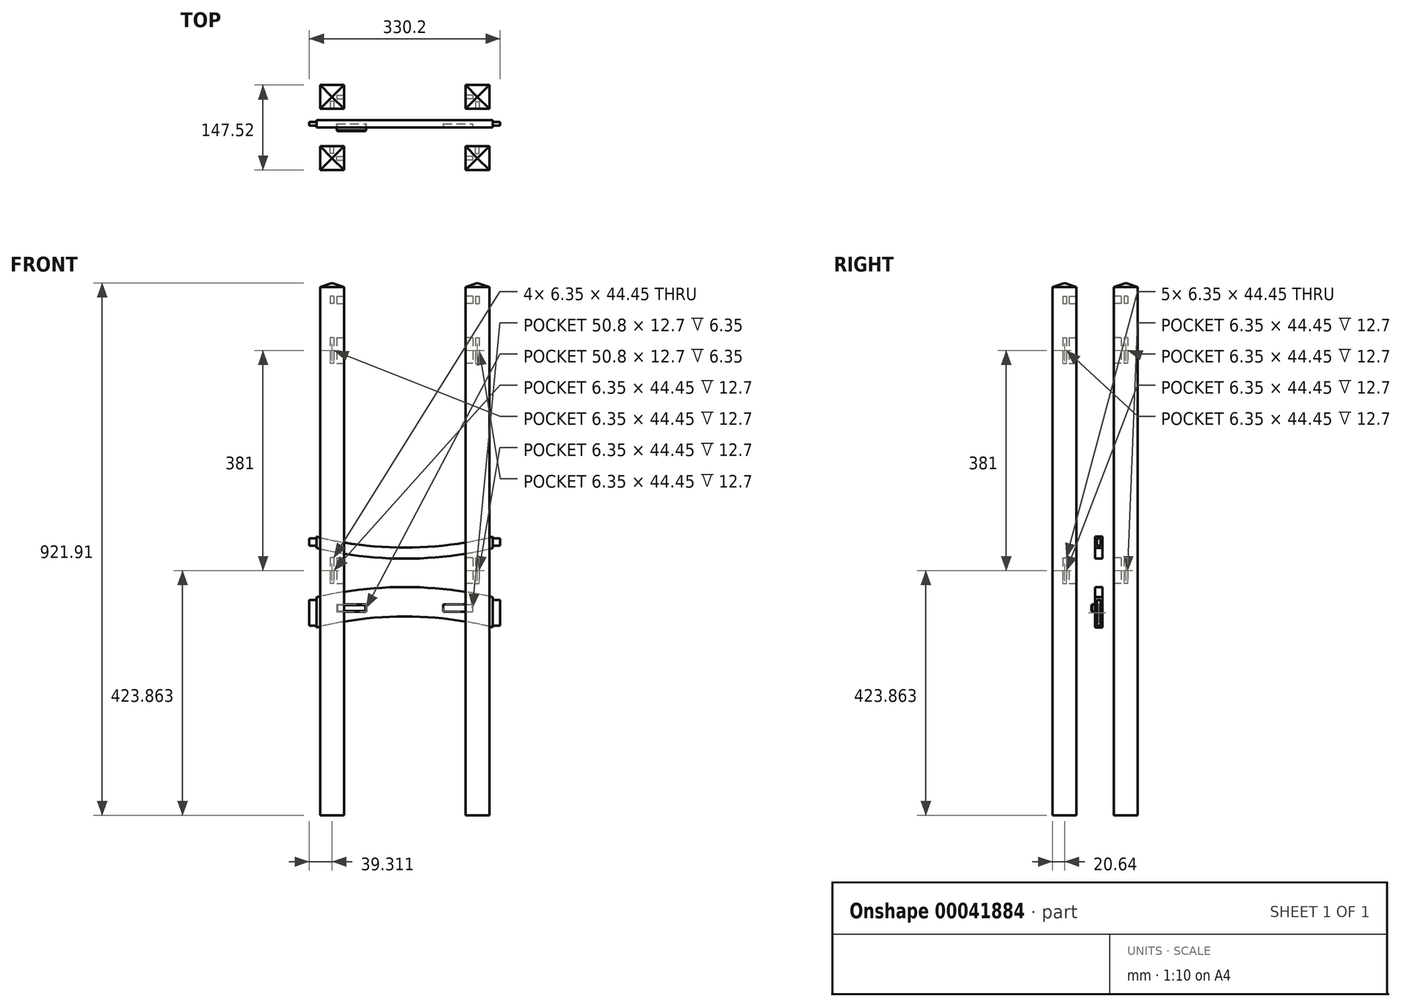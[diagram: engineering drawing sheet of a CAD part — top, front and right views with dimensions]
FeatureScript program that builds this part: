
annotation { "Feature Type Name" : "Feature", "Feature Type Description" : "" }
export const myFeature = defineFeature(function(context is Context, id is Id, definition is map)
    precondition{}
    {
        {
            var Q0;
            Q0=qCreatedBy(makeId("Front.planeOp"),FACE);
            var sketch = newSketch(context, id + "F0", { "sketchPlane" : qUnion([Q0])});
            skLineSegment(sketch, "E0.left", {"start": v(-165.1, 22.23) * mm, "end": v(-165.1, 9.53) * mm});
            skLineSegment(sketch, "E0.right", {"start": v(165.1, 22.23) * mm, "end": v(165.1, 9.53) * mm});
            skLineSegment(sketch, "E1", {"start": v(-152.4, 25.4) * mm, "end": v(-152.4, 22.23) * mm});
            skLineSegment(sketch, "E2", {"start": v(152.4, 25.4) * mm, "end": v(152.4, 22.23) * mm});
            skLineSegment(sketch, "E3.bottom", {"start": v(-165.1, 22.23) * mm, "end": v(-152.4, 22.23) * mm});
            skLineSegment(sketch, "E3.top", {"start": v(-165.1, 9.53) * mm, "end": v(-152.4, 9.53) * mm});
            skLineSegment(sketch, "E4.bottom", {"start": v(165.1, 22.23) * mm, "end": v(152.4, 22.23) * mm});
            skLineSegment(sketch, "E4.top", {"start": v(165.1, 9.53) * mm, "end": v(152.4, 9.53) * mm});
            skLineSegment(sketch, "E5.trimOffspring", {"start": v(-152.4, 9.53) * mm, "end": v(-152.4, 5.76) * mm});
            skPoint(sketch, "E6.orphan", {"position": v(-165.1, -25.4) * mm});
            skLineSegment(sketch, "E7.trimOffspring", {"start": v(152.4, 9.53) * mm, "end": v(152.4, 5.76) * mm});
            skLineSegment(sketch, "E8", {"start": v(-154.76, 6.35) * mm, "end": v(154.76, 6.35) * mm, "construction": true});
            skLineSegment(sketch, "E9", {"start": v(0, 25.4) * mm, "end": v(0, -25.4) * mm, "construction": true});
            skPoint(sketch, "E10", {"position": v(0, 6.35) * mm});
            skArc(sketch, "E11", {"start": v(-152.4, 25.4) * mm, "mid": v(0, 6.35) * mm, "end": v(152.4, 25.4) * mm});
            skArc(sketch, "E12.trimOffspring", {"start": v(-152.4, 5.76) * mm, "mid": v(0, -12.7) * mm, "end": v(152.4, 5.76) * mm});
            skPoint(sketch, "E13.orphan", {"position": v(-152.4, -25.4) * mm});
            skPoint(sketch, "E14.orphan", {"position": v(152.4, -25.4) * mm});
            skSolve(sketch);
        }
        {
            var Q0;
            Q0 = qSketchRegion(id + "F0", true);
            extrude(context, id + "F1", {"entities" : qUnion([Q0]), "oppositeDirection" : true, "depth" : 12.7 * mm});
        }
        {
            var Q0;
            Q0=qCreatedBy(makeId("Front.planeOp"),FACE);
            var sketch = newSketch(context, id + "F2", { "sketchPlane" : qUnion([Q0])});
            skLineSegment(sketch, "E15.left", {"start": v(-165.1, -84.02) * mm, "end": v(-165.1, -128.47) * mm});
            skLineSegment(sketch, "E15.right", {"start": v(165.1, -84.02) * mm, "end": v(165.1, -128.47) * mm});
            skLineSegment(sketch, "E16", {"start": v(-152.4, -79.36) * mm, "end": v(-152.4, -84.02) * mm});
            skLineSegment(sketch, "E17", {"start": v(152.4, -79.36) * mm, "end": v(152.4, -84.02) * mm});
            skLineSegment(sketch, "E18", {"start": v(152.4, -84.02) * mm, "end": v(165.1, -84.02) * mm});
            skLineSegment(sketch, "E19", {"start": v(152.4, -128.47) * mm, "end": v(165.1, -128.47) * mm});
            skLineSegment(sketch, "E20", {"start": v(-165.1, -128.47) * mm, "end": v(-152.4, -128.47) * mm});
            skLineSegment(sketch, "E21", {"start": v(-165.1, -84.02) * mm, "end": v(-152.4, -84.02) * mm});
            skPoint(sketch, "E22.orphan", {"position": v(165.1, -131.64) * mm});
            skLineSegment(sketch, "E23.0", {"start": v(-152.4, -112.6) * mm, "end": v(152.4, -112.6) * mm, "construction": true});
            skLineSegment(sketch, "E24", {"start": v(0, -112.6) * mm, "end": v(0, -131.64) * mm, "construction": true});
            skArc(sketch, "E25", {"start": v(152.4, -131.64) * mm, "mid": v(0, -112.6) * mm, "end": v(-152.4, -131.64) * mm});
            skArc(sketch, "E26.0", {"start": v(152.4, -79.36) * mm, "mid": v(0, -61.8) * mm, "end": v(-152.4, -79.36) * mm});
            skLineSegment(sketch, "E27.trimOffspring", {"start": v(-152.4, -128.47) * mm, "end": v(-152.4, -131.64) * mm});
            skLineSegment(sketch, "E28.trimOffspring", {"start": v(152.4, -128.47) * mm, "end": v(152.4, -131.64) * mm});
            skSolve(sketch);
        }
        {
            var Q0;
            Q0 = qSketchRegion(id + "F2", true);
            extrude(context, id + "F3", {"entities" : qUnion([Q0]), "oppositeDirection" : true, "depth" : 12.7 * mm});
        }
        {
            var Q0;
            Q0=makeQuery(id+"F3.opExtrude","CAP_FACE",FACE,{"disambiguationData":[OSD([sQuery(id+"F2.wireOp",EDGE,"E15.left"),sQuery(id+"F2.wireOp",EDGE,"E15.right"),sQuery(id+"F2.wireOp",EDGE,"E16"),sQuery(id+"F2.wireOp",EDGE,"E17"),sQuery(id+"F2.wireOp",EDGE,"E18"),sQuery(id+"F2.wireOp",EDGE,"E19"),sQuery(id+"F2.wireOp",EDGE,"E20"),sQuery(id+"F2.wireOp",EDGE,"E21"),sQuery(id+"F2.wireOp",EDGE,"E25"),sQuery(id+"F2.wireOp",EDGE,"E26.0"),sQuery(id+"F2.wireOp",EDGE,"E27.trimOffspring"),sQuery(id+"F2.wireOp",EDGE,"E28.trimOffspring")])],"isStart":true});
            var sketch = newSketch(context, id + "F4", { "sketchPlane" : qUnion([Q0])});
            skLineSegment(sketch, "E29.bottom", {"start": v(-117.47, -91.95) * mm, "end": v(-66.67, -91.95) * mm});
            skLineSegment(sketch, "E29.top", {"start": v(-117.47, -104.65) * mm, "end": v(-66.67, -104.65) * mm});
            skLineSegment(sketch, "E29.left", {"start": v(-117.47, -91.95) * mm, "end": v(-117.47, -104.65) * mm});
            skLineSegment(sketch, "E29.right", {"start": v(-66.67, -91.95) * mm, "end": v(-66.67, -104.65) * mm});
            skPoint(sketch, "E30.oppositeSnap0", {"position": v(-92.07, -104.65) * mm});
            skLineSegment(sketch, "E30.bottom", {"start": v(66.68, -91.95) * mm, "end": v(117.48, -91.95) * mm});
            skLineSegment(sketch, "E30.top", {"start": v(66.68, -104.65) * mm, "end": v(117.48, -104.65) * mm});
            skLineSegment(sketch, "E30.left", {"start": v(66.68, -91.95) * mm, "end": v(66.68, -104.65) * mm});
            skLineSegment(sketch, "E30.right", {"start": v(117.48, -91.95) * mm, "end": v(117.48, -104.65) * mm});
            skSolve(sketch);
        }
        {
            var Q0;
            Q0 = qSketchRegion(id + "F4", true);
            extrude(context, id + "F5", {"entities" : qUnion([Q0]), "operationType" : NewBodyOperationType.REMOVE, "oppositeDirection" : true, "depth" : 6.35 * mm});
        }
        {
            var Q0;
            Q0=qCreatedBy(makeId("Top.planeOp"),FACE);
            var sketch = newSketch(context, id + "F6", { "sketchPlane" : qUnion([Q0])});
            skLineSegment(sketch, "E31.bottom", {"start": v(-146.43, -32.48) * mm, "end": v(-105.15, -32.48) * mm});
            skLineSegment(sketch, "E31.top", {"start": v(-146.43, -73.76) * mm, "end": v(-105.15, -73.76) * mm});
            skLineSegment(sketch, "E31.left", {"start": v(-146.43, -32.48) * mm, "end": v(-146.43, -73.76) * mm});
            skLineSegment(sketch, "E31.right", {"start": v(-105.15, -32.48) * mm, "end": v(-105.15, -73.76) * mm});
            skSolve(sketch);
        }
        {
            var Q0;
            Q0 = qSketchRegion(id + "F6", true);
            extrude(context, id + "F7", {"entities" : qUnion([Q0]), "endBound" : BoundingType.SYMMETRIC, "depth" : 914.4 * mm});
        }
        {
            var Q0;
            Q0=makeQuery(id+"F7.opExtrude","SWEPT_FACE",FACE,{"disambiguationData":[OSD([sQuery(id+"F6.wireOp",EDGE,"E31.right")])]});
            var sketch = newSketch(context, id + "F8", { "sketchPlane" : qUnion([Q0])});
            skLineSegment(sketch, "E32.bottom", {"start": v(-56.3, 441.33) * mm, "end": v(-49.94, 441.33) * mm});
            skLineSegment(sketch, "E32.top", {"start": v(-56.3, 428.63) * mm, "end": v(-49.94, 428.63) * mm});
            skLineSegment(sketch, "E32.left", {"start": v(-56.3, 441.33) * mm, "end": v(-56.3, 428.63) * mm});
            skLineSegment(sketch, "E32.right", {"start": v(-49.94, 441.33) * mm, "end": v(-49.94, 428.63) * mm});
            skLineSegment(sketch, "E33.bottom", {"start": v(-56.3, 369.89) * mm, "end": v(-49.94, 369.89) * mm});
            skLineSegment(sketch, "E33.top", {"start": v(-56.3, 325.44) * mm, "end": v(-49.94, 325.44) * mm});
            skLineSegment(sketch, "E33.left", {"start": v(-56.3, 369.89) * mm, "end": v(-56.3, 325.44) * mm});
            skLineSegment(sketch, "E33.right", {"start": v(-49.94, 369.89) * mm, "end": v(-49.94, 325.44) * mm});
            skLineSegment(sketch, "E34.bottom", {"start": v(-56.3, -11.11) * mm, "end": v(-49.94, -11.11) * mm});
            skLineSegment(sketch, "E34.top", {"start": v(-56.3, -55.56) * mm, "end": v(-49.94, -55.56) * mm});
            skLineSegment(sketch, "E34.left", {"start": v(-56.3, -11.11) * mm, "end": v(-56.3, -55.56) * mm});
            skLineSegment(sketch, "E34.right", {"start": v(-49.94, -11.11) * mm, "end": v(-49.94, -55.56) * mm});
            skPoint(sketch, "E35", {"position": v(-53.12, 441.33) * mm});
            skSolve(sketch);
        }
        {
            var Q0;
            Q0=makeQuery(id+"F7.opExtrude","CAP_FACE",FACE,{"disambiguationData":[OSD([sQuery(id+"F6.wireOp",EDGE,"E31.bottom"),sQuery(id+"F6.wireOp",EDGE,"E31.top"),sQuery(id+"F6.wireOp",EDGE,"E31.left"),sQuery(id+"F6.wireOp",EDGE,"E31.right")])],"isStart":false});
            extrude(context, id + "F9", {"entities" : qUnion([Q0]), "operationType" : NewBodyOperationType.ADD, "depth" : 7.94 * mm, "hasDraft" : true, "draftAngle" : 70 * degree, "draftPullDirection" : true});
        }
        {
            var Q0;
            Q0=makeQuery(id+"F7.opExtrude","SWEPT_FACE",FACE,{"disambiguationData":[OSD([sQuery(id+"F6.wireOp",EDGE,"E31.bottom")])]});
            var sketch = newSketch(context, id + "F10", { "sketchPlane" : qUnion([Q0])});
            skLineSegment(sketch, "E36.bottom", {"start": v(122.61, 441.33) * mm, "end": v(128.96, 441.33) * mm});
            skLineSegment(sketch, "E36.top", {"start": v(122.61, 428.63) * mm, "end": v(128.96, 428.63) * mm});
            skLineSegment(sketch, "E36.left", {"start": v(122.61, 441.33) * mm, "end": v(122.61, 428.63) * mm});
            skLineSegment(sketch, "E36.right", {"start": v(128.96, 441.33) * mm, "end": v(128.96, 428.63) * mm});
            skLineSegment(sketch, "E37.bottom", {"start": v(122.61, 369.89) * mm, "end": v(128.96, 369.89) * mm});
            skLineSegment(sketch, "E37.top", {"start": v(122.61, 325.44) * mm, "end": v(128.96, 325.44) * mm});
            skLineSegment(sketch, "E37.left", {"start": v(122.61, 369.89) * mm, "end": v(122.61, 325.44) * mm});
            skLineSegment(sketch, "E37.right", {"start": v(128.96, 369.89) * mm, "end": v(128.96, 325.44) * mm});
            skLineSegment(sketch, "E38.bottom", {"start": v(122.61, -11.11) * mm, "end": v(128.96, -11.11) * mm});
            skLineSegment(sketch, "E38.top", {"start": v(122.61, -55.56) * mm, "end": v(128.96, -55.56) * mm});
            skLineSegment(sketch, "E38.left", {"start": v(122.61, -11.11) * mm, "end": v(122.61, -55.56) * mm});
            skLineSegment(sketch, "E38.right", {"start": v(128.96, -11.11) * mm, "end": v(128.96, -55.56) * mm});
            skPoint(sketch, "E39", {"position": v(125.79, 441.33) * mm});
            skLineSegment(sketch, "E40", {"start": v(125.79, 457.2) * mm, "end": v(125.79, 391.14) * mm, "construction": true});
            skSolve(sketch);
        }
        {
            var Q0;
            Q0=makeQuery(id+"F1.opExtrude","CAP_FACE",FACE,{"disambiguationData":[OSD([sQuery(id+"F0.wireOp",EDGE,"E1"),sQuery(id+"F0.wireOp",EDGE,"E2"),sQuery(id+"F0.wireOp",EDGE,"E3.bottom"),sQuery(id+"F0.wireOp",EDGE,"E3.top"),sQuery(id+"F0.wireOp",EDGE,"E0.left"),sQuery(id+"F0.wireOp",EDGE,"E4.bottom"),sQuery(id+"F0.wireOp",EDGE,"E4.top"),sQuery(id+"F0.wireOp",EDGE,"E0.right"),sQuery(id+"F0.wireOp",EDGE,"E5.trimOffspring"),sQuery(id+"F0.wireOp",EDGE,"E7.trimOffspring"),sQuery(id+"F0.wireOp",EDGE,"E11"),sQuery(id+"F0.wireOp",EDGE,"E12.trimOffspring")])],"isStart":true});
            var sketch = newSketch(context, id + "F11", { "sketchPlane" : qUnion([Q0])});
            skLineSegment(sketch, "E41", {"start": v(152.4, 22.23) * mm, "end": v(152.4, 9.53) * mm});
            skLineSegment(sketch, "E42", {"start": v(-152.4, 22.23) * mm, "end": v(-152.4, 9.53) * mm});
            skSolve(sketch);
        }
        {
            var Q0;
            Q0 = qSketchRegion(id + "F10", true);
            extrude(context, id + "F12", {"entities" : qUnion([Q0]), "operationType" : NewBodyOperationType.REMOVE, "oppositeDirection" : true, "depth" : 12.7 * mm});
        }
        {
            var Q0;
            Q0=makeQuery(id+"F11.imprint","IMPRINT",FACE,{"disambiguationData":[TD([[makeQuery(id+"F11.imprint","IMPRINT",EDGE,{"derivedFrom":sQuery(id+"F11.wireOp",EDGE,"E42")}),-1.0]])]});
            var Q1;
            Q1=makeQuery(id+"F11.imprint","IMPRINT",FACE,{"disambiguationData":[TD([[makeQuery(id+"F11.imprint","IMPRINT",EDGE,{"derivedFrom":sQuery(id+"F11.wireOp",EDGE,"E41")}),1.0]])]});
            extrude(context, id + "F13", {"entities" : qUnion([Q0, Q1]), "operationType" : NewBodyOperationType.REMOVE, "oppositeDirection" : true, "depth" : 3.17 * mm});
        }
        {
            var Q0;
            Q0=makeQuery(id+"F1.opExtrude","CAP_FACE",FACE,{"disambiguationData":[OSD([sQuery(id+"F0.wireOp",EDGE,"E1"),sQuery(id+"F0.wireOp",EDGE,"E2"),sQuery(id+"F0.wireOp",EDGE,"E3.bottom"),sQuery(id+"F0.wireOp",EDGE,"E3.top"),sQuery(id+"F0.wireOp",EDGE,"E0.left"),sQuery(id+"F0.wireOp",EDGE,"E4.bottom"),sQuery(id+"F0.wireOp",EDGE,"E4.top"),sQuery(id+"F0.wireOp",EDGE,"E0.right"),sQuery(id+"F0.wireOp",EDGE,"E5.trimOffspring"),sQuery(id+"F0.wireOp",EDGE,"E7.trimOffspring"),sQuery(id+"F0.wireOp",EDGE,"E11"),sQuery(id+"F0.wireOp",EDGE,"E12.trimOffspring")])],"isStart":false});
            var sketch = newSketch(context, id + "F14", { "sketchPlane" : qUnion([Q0])});
            skLineSegment(sketch, "E43", {"start": v(-152.4, 22.23) * mm, "end": v(-152.4, 9.53) * mm});
            skLineSegment(sketch, "E44", {"start": v(152.4, 22.23) * mm, "end": v(152.4, 9.53) * mm});
            skSolve(sketch);
        }
        {
            var Q0;
            Q0=makeQuery(id+"F14.imprint","IMPRINT",FACE,{"disambiguationData":[TD([[makeQuery(id+"F14.imprint","IMPRINT",EDGE,{"derivedFrom":sQuery(id+"F14.wireOp",EDGE,"E43")}),-1.0]])]});
            var Q1;
            Q1=makeQuery(id+"F14.imprint","IMPRINT",FACE,{"disambiguationData":[TD([[makeQuery(id+"F14.imprint","IMPRINT",EDGE,{"derivedFrom":sQuery(id+"F14.wireOp",EDGE,"E44")}),1.0]])]});
            extrude(context, id + "F15", {"entities" : qUnion([Q0, Q1]), "operationType" : NewBodyOperationType.REMOVE, "oppositeDirection" : true, "depth" : 3.17 * mm});
        }
        {
            var Q0;
            Q0=makeQuery(id+"F3.opExtrude","CAP_FACE",FACE,{"disambiguationData":[OSD([sQuery(id+"F2.wireOp",EDGE,"E15.left"),sQuery(id+"F2.wireOp",EDGE,"E15.right"),sQuery(id+"F2.wireOp",EDGE,"E16"),sQuery(id+"F2.wireOp",EDGE,"E17"),sQuery(id+"F2.wireOp",EDGE,"E18"),sQuery(id+"F2.wireOp",EDGE,"E19"),sQuery(id+"F2.wireOp",EDGE,"E20"),sQuery(id+"F2.wireOp",EDGE,"E21"),sQuery(id+"F2.wireOp",EDGE,"E25"),sQuery(id+"F2.wireOp",EDGE,"E26.0"),sQuery(id+"F2.wireOp",EDGE,"E27.trimOffspring"),sQuery(id+"F2.wireOp",EDGE,"E28.trimOffspring")])],"isStart":false});
            var sketch = newSketch(context, id + "F16", { "sketchPlane" : qUnion([Q0])});
            skLineSegment(sketch, "E45", {"start": v(-152.4, -84.02) * mm, "end": v(-152.4, -128.47) * mm});
            skLineSegment(sketch, "E46", {"start": v(152.4, -84.02) * mm, "end": v(152.4, -128.47) * mm});
            skSolve(sketch);
        }
        {
            var Q0;
            Q0=makeQuery(id+"F16.imprint","IMPRINT",FACE,{"disambiguationData":[TD([[makeQuery(id+"F16.imprint","IMPRINT",EDGE,{"derivedFrom":sQuery(id+"F16.wireOp",EDGE,"E45")}),-1.0]])]});
            var Q1;
            Q1=makeQuery(id+"F16.imprint","IMPRINT",FACE,{"disambiguationData":[TD([[makeQuery(id+"F16.imprint","IMPRINT",EDGE,{"derivedFrom":sQuery(id+"F16.wireOp",EDGE,"E46")}),1.0]])]});
            extrude(context, id + "F17", {"entities" : qUnion([Q0, Q1]), "operationType" : NewBodyOperationType.REMOVE, "oppositeDirection" : true, "depth" : 3.17 * mm});
        }
        {
            var Q0;
            Q0=makeQuery(id+"F3.opExtrude","CAP_FACE",FACE,{"disambiguationData":[OSD([sQuery(id+"F2.wireOp",EDGE,"E15.left"),sQuery(id+"F2.wireOp",EDGE,"E15.right"),sQuery(id+"F2.wireOp",EDGE,"E16"),sQuery(id+"F2.wireOp",EDGE,"E17"),sQuery(id+"F2.wireOp",EDGE,"E18"),sQuery(id+"F2.wireOp",EDGE,"E19"),sQuery(id+"F2.wireOp",EDGE,"E20"),sQuery(id+"F2.wireOp",EDGE,"E21"),sQuery(id+"F2.wireOp",EDGE,"E25"),sQuery(id+"F2.wireOp",EDGE,"E26.0"),sQuery(id+"F2.wireOp",EDGE,"E27.trimOffspring"),sQuery(id+"F2.wireOp",EDGE,"E28.trimOffspring")])],"isStart":true});
            var sketch = newSketch(context, id + "F18", { "sketchPlane" : qUnion([Q0])});
            skLineSegment(sketch, "E47", {"start": v(-152.4, -84.02) * mm, "end": v(-152.4, -128.47) * mm});
            skLineSegment(sketch, "E48", {"start": v(152.4, -84.02) * mm, "end": v(152.4, -128.47) * mm});
            skSolve(sketch);
        }
        {
            var Q0;
            Q0=makeQuery(id+"F18.imprint","IMPRINT",FACE,{"disambiguationData":[TD([[makeQuery(id+"F18.imprint","IMPRINT",EDGE,{"derivedFrom":sQuery(id+"F18.wireOp",EDGE,"E47")}),-1.0]])]});
            var Q1;
            Q1=makeQuery(id+"F18.imprint","IMPRINT",FACE,{"disambiguationData":[TD([[makeQuery(id+"F18.imprint","IMPRINT",EDGE,{"derivedFrom":sQuery(id+"F18.wireOp",EDGE,"E48")}),1.0]])]});
            extrude(context, id + "F19", {"entities" : qUnion([Q0, Q1]), "operationType" : NewBodyOperationType.REMOVE, "oppositeDirection" : true, "depth" : 3.17 * mm});
        }
        {
            var Q0;
            Q0 = qSketchRegion(id + "F8", true);
            extrude(context, id + "F20", {"entities" : qUnion([Q0]), "operationType" : NewBodyOperationType.REMOVE, "oppositeDirection" : true, "depth" : 12.7 * mm});
        }
        {
            var Q0;
            Q0=makeQuery(id+"F7.opExtrude","SWEPT_BODY",BODY,{"disambiguationData":[OSD([sQuery(id+"F6.wireOp",EDGE,"E31.bottom"),sQuery(id+"F6.wireOp",EDGE,"E31.top"),sQuery(id+"F6.wireOp",EDGE,"E31.left"),sQuery(id+"F6.wireOp",EDGE,"E31.right")])]});
            var Q1;
            Q1=qCreatedBy(makeId("Right.planeOp"),FACE);
            mirror(context, id + "F21", {"entities" : qUnion([Q0]), "mirrorPlane" : qUnion([Q1])});
        }
        {
            var Q0;
            Q0=makeQuery(id+"F21.opPattern","COPY",BODY,{"derivedFrom":makeQuery(id+"F7.opExtrude","SWEPT_BODY",BODY,{"disambiguationData":[OSD([sQuery(id+"F6.wireOp",EDGE,"E31.bottom"),sQuery(id+"F6.wireOp",EDGE,"E31.top"),sQuery(id+"F6.wireOp",EDGE,"E31.left"),sQuery(id+"F6.wireOp",EDGE,"E31.right")])]}),"instanceName":"1"});
            var Q1;
            Q1=makeQuery(id+"F7.opExtrude","SWEPT_BODY",BODY,{"disambiguationData":[OSD([sQuery(id+"F6.wireOp",EDGE,"E31.bottom"),sQuery(id+"F6.wireOp",EDGE,"E31.top"),sQuery(id+"F6.wireOp",EDGE,"E31.left"),sQuery(id+"F6.wireOp",EDGE,"E31.right")])]});
            var Q2;
            Q2=qCreatedBy(makeId("Front.planeOp"),FACE);
            mirror(context, id + "F22", {"entities" : qUnion([Q0, Q1]), "mirrorPlane" : qUnion([Q2])});
        }
        {
            var Q0;
            Q0=makeQuery(id+"F5.boolean.opBoolean","COPY",FACE,{"derivedFrom":makeQuery(id+"F5.opExtrude","CAP_FACE",FACE,{"disambiguationData":[OSD([sQuery(id+"F4.wireOp",EDGE,"E29.bottom"),sQuery(id+"F4.wireOp",EDGE,"E29.top"),sQuery(id+"F4.wireOp",EDGE,"E29.left"),sQuery(id+"F4.wireOp",EDGE,"E29.right")])],"isStart":false})});
            var sketch = newSketch(context, id + "F23", { "sketchPlane" : qUnion([Q0])});
            skLineSegment(sketch, "E49.0", {"start": v(-117.47, -91.95) * mm, "end": v(-66.67, -91.95) * mm});
            skLineSegment(sketch, "E49.1", {"start": v(66.68, -91.95) * mm, "end": v(117.48, -91.95) * mm});
            skLineSegment(sketch, "E50", {"start": v(-117.47, -91.95) * mm, "end": v(-117.47, -104.65) * mm});
            skLineSegment(sketch, "E51", {"start": v(-117.47, -104.65) * mm, "end": v(-66.67, -104.65) * mm});
            skLineSegment(sketch, "E52", {"start": v(-66.67, -104.65) * mm, "end": v(-66.67, -91.95) * mm});
            skLineSegment(sketch, "E53", {"start": v(66.68, -91.95) * mm, "end": v(66.68, -104.65) * mm});
            skLineSegment(sketch, "E54", {"start": v(66.68, -104.65) * mm, "end": v(117.48, -104.65) * mm});
            skLineSegment(sketch, "E55", {"start": v(117.48, -104.65) * mm, "end": v(117.48, -91.95) * mm});
            skSolve(sketch);
        }
        {
            var Q0;
            Q0 = qSketchRegion(id + "F23", true);
            extrude(context, id + "F24", {"entities" : qUnion([Q0]), "depth" : 12.7 * mm});
        }
        {
            var Q0;
            Q0=makeQuery(id+"F24.opExtrude","CAP_EDGE",EDGE,{"disambiguationData":[OSD([sQuery(id+"F23.wireOp",EDGE,"E49.0")])],"isStart":false});
            var Q1;
            Q1=makeQuery(id+"F24.opExtrude","CAP_EDGE",EDGE,{"disambiguationData":[OSD([sQuery(id+"F23.wireOp",EDGE,"E50")])],"isStart":false});
            var Q2;
            Q2=makeQuery(id+"F24.opExtrude","CAP_EDGE",EDGE,{"disambiguationData":[OSD([sQuery(id+"F23.wireOp",EDGE,"E51")])],"isStart":false});
            var Q3;
            Q3=makeQuery(id+"F24.opExtrude","CAP_EDGE",EDGE,{"disambiguationData":[OSD([sQuery(id+"F23.wireOp",EDGE,"E52")])],"isStart":false});
            chamfer(context, id + "F25", {"entities" : qUnion([Q0, Q1, Q2, Q3]), "width" : 1.27 * mm, "tangentPropagation" : true});
        }
        {
            var Q0;
            Q0=makeQuery(id+"F24.opExtrude","CAP_EDGE",EDGE,{"disambiguationData":[OSD([sQuery(id+"F23.wireOp",EDGE,"E49.1")])],"isStart":false});
            var Q1;
            Q1=makeQuery(id+"F24.opExtrude","CAP_EDGE",EDGE,{"disambiguationData":[OSD([sQuery(id+"F23.wireOp",EDGE,"E53")])],"isStart":false});
            var Q2;
            Q2=makeQuery(id+"F24.opExtrude","CAP_EDGE",EDGE,{"disambiguationData":[OSD([sQuery(id+"F23.wireOp",EDGE,"E54")])],"isStart":false});
            var Q3;
            Q3=makeQuery(id+"F24.opExtrude","CAP_EDGE",EDGE,{"disambiguationData":[OSD([sQuery(id+"F23.wireOp",EDGE,"E55")])],"isStart":false});
            chamfer(context, id + "F26", {"entities" : qUnion([Q0, Q1, Q2, Q3]), "width" : 2.54 * mm, "tangentPropagation" : true});
        }
        {
            var Q0;
            Q0=makeQuery(id+"F24.opExtrude","SWEPT_BODY",BODY,{"disambiguationData":[OSD([sQuery(id+"F23.wireOp",EDGE,"E49.1"),sQuery(id+"F23.wireOp",EDGE,"E53"),sQuery(id+"F23.wireOp",EDGE,"E54"),sQuery(id+"F23.wireOp",EDGE,"E55")])]});
            deleteBodies(context, id + "F27", {"entities" : qUnion([Q0])});
        }
    });
